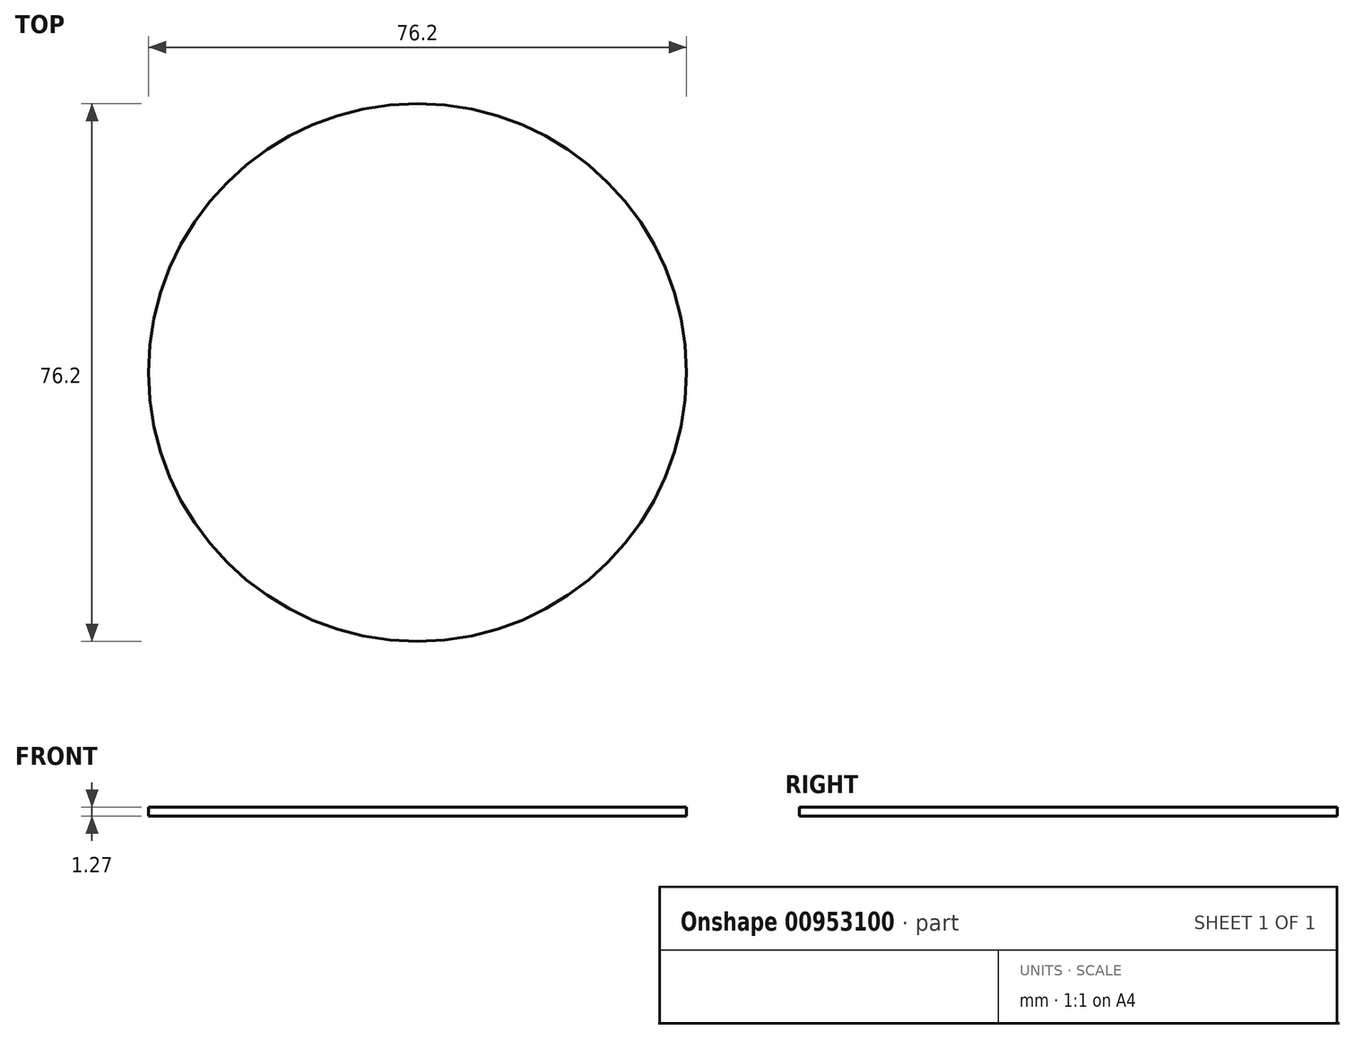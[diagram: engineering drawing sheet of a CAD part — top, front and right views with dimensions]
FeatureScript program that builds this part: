
annotation { "Feature Type Name" : "Feature", "Feature Type Description" : "" }
export const myFeature = defineFeature(function(context is Context, id is Id, definition is map)
    precondition{}
    {
        {
            var Q0;
            Q0=qCreatedBy(makeId("Top.planeOp"),FACE);
            var sketch = newSketch(context, id + "F0", { "sketchPlane" : qUnion([Q0])});
            skCircle(sketch, "E0", {"center": v(0, 0) * mm, "radius": 38.1 * mm});
            skSolve(sketch);
        }
        {
            var Q0;
            Q0 = qSketchRegion(id + "F0", true);
            extrude(context, id + "F1", {"entities" : qUnion([Q0]), "oppositeDirection" : true, "depth" : 1.27 * mm, "offsetDistance" : 25.4 * mm});
        }
    });
